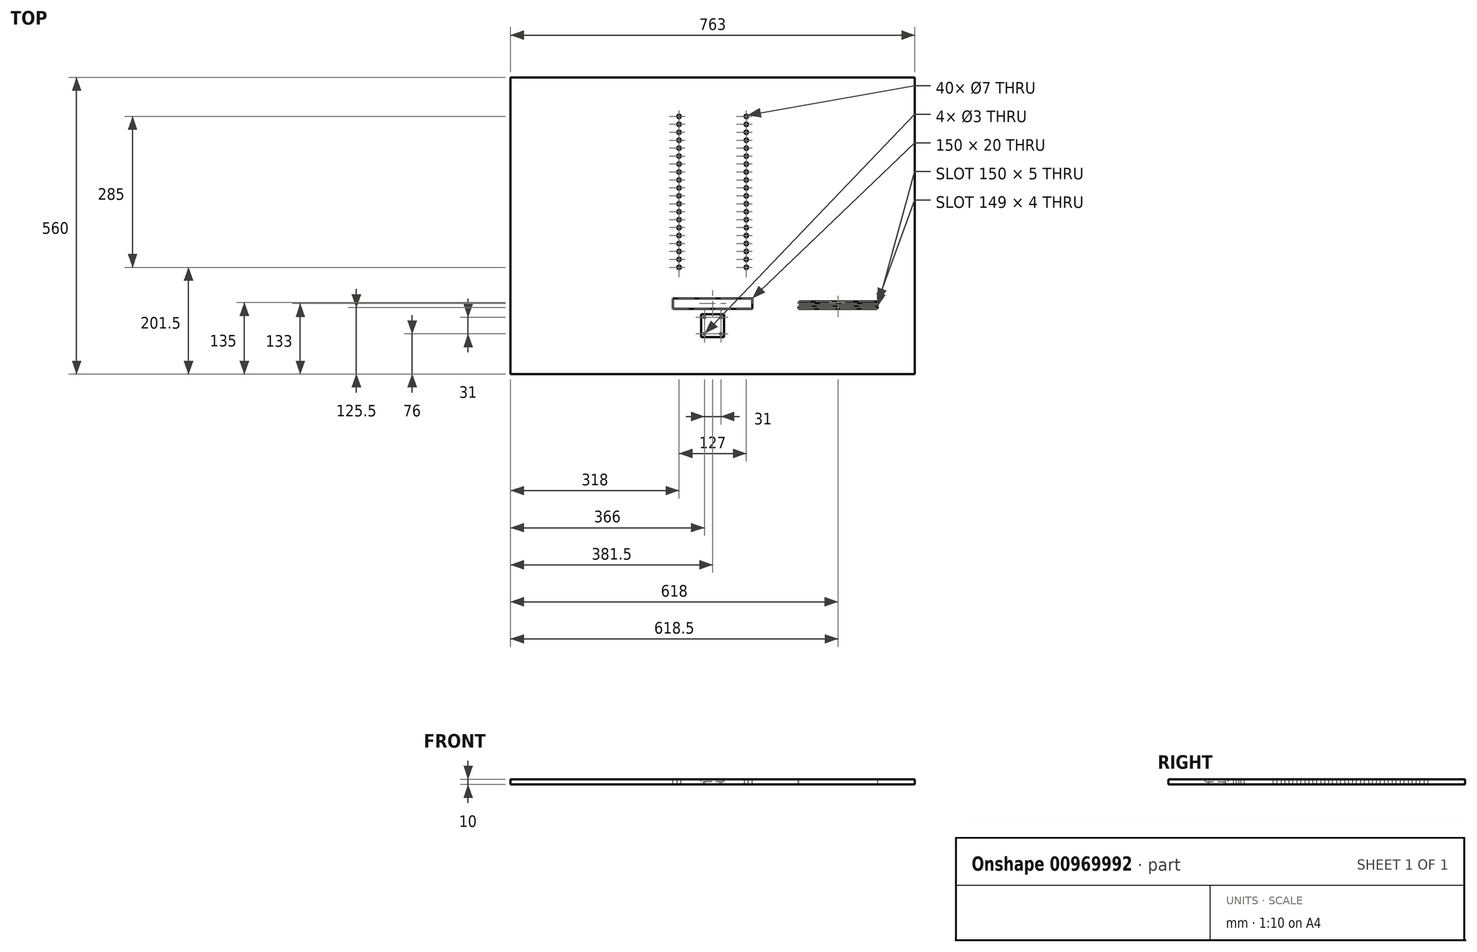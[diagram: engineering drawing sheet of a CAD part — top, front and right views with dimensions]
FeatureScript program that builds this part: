
annotation { "Feature Type Name" : "Feature", "Feature Type Description" : "" }
export const myFeature = defineFeature(function(context is Context, id is Id, definition is map)
    precondition{}
    {
        {
            var Q0;
            Q0=qCreatedBy(makeId("Top.planeOp"),FACE);
            var sketch = newSketch(context, id + "F0", { "sketchPlane" : qUnion([Q0])});
            skLineSegment(sketch, "E0.bottom", {"start": v(381.5, -280) * mm, "end": v(-381.5, -280) * mm});
            skLineSegment(sketch, "E0.top", {"start": v(381.5, 280) * mm, "end": v(-381.5, 280) * mm});
            skLineSegment(sketch, "E0.left", {"start": v(381.5, -280) * mm, "end": v(381.5, 280) * mm});
            skLineSegment(sketch, "E0.right", {"start": v(-381.5, -280) * mm, "end": v(-381.5, 280) * mm});
            skPoint(sketch, "E0.middle", {"position": v(0, 0) * mm});
            skSolve(sketch);
        }
        {
            var Q0;
            Q0=qSketchRegion(id+"F0",true);
            extrude(context, id + "F1", {"entities" : qUnion([Q0]), "depth" : 10 * mm, "offsetDistance" : 25 * mm});
        }
        {
            var Q0;
            Q0=makeQuery(id+"F1.opExtrude","CAP_FACE",FACE,{"disambiguationData":[OSD([sQuery(id+"F0.wireOp",EDGE,"E0.bottom"),sQuery(id+"F0.wireOp",EDGE,"E0.top"),sQuery(id+"F0.wireOp",EDGE,"E0.left"),sQuery(id+"F0.wireOp",EDGE,"E0.right")])],"isStart":false});
            var sketch = newSketch(context, id + "F2", { "sketchPlane" : qUnion([Q0])});
            skLineSegment(sketch, "E1", {"start": v(0, 280) * mm, "end": v(0, -280) * mm, "construction": true});
            skCircle(sketch, "E2", {"center": v(-63.5, 206.5) * mm, "radius": 3.5 * mm});
            skCircle(sketch, "E3.0.1.0", {"center": v(-63.5, 191.5) * mm, "radius": 3.5 * mm});
            skCircle(sketch, "E3.0.2.0", {"center": v(-63.5, 176.5) * mm, "radius": 3.5 * mm});
            skCircle(sketch, "E3.0.3.0", {"center": v(-63.5, 161.5) * mm, "radius": 3.5 * mm});
            skCircle(sketch, "E3.0.4.0", {"center": v(-63.5, 146.5) * mm, "radius": 3.5 * mm});
            skCircle(sketch, "E3.0.5.0", {"center": v(-63.5, 131.5) * mm, "radius": 3.5 * mm});
            skCircle(sketch, "E3.0.6.0", {"center": v(-63.5, 116.5) * mm, "radius": 3.5 * mm});
            skCircle(sketch, "E3.0.7.0", {"center": v(-63.5, 101.5) * mm, "radius": 3.5 * mm});
            skCircle(sketch, "E3.0.8.0", {"center": v(-63.5, 86.5) * mm, "radius": 3.5 * mm});
            skCircle(sketch, "E3.0.9.0", {"center": v(-63.5, 71.5) * mm, "radius": 3.5 * mm});
            skCircle(sketch, "E3.0.10.0", {"center": v(-63.5, 56.5) * mm, "radius": 3.5 * mm});
            skCircle(sketch, "E3.0.11.0", {"center": v(-63.5, 41.5) * mm, "radius": 3.5 * mm});
            skCircle(sketch, "E3.0.12.0", {"center": v(-63.5, 26.5) * mm, "radius": 3.5 * mm});
            skCircle(sketch, "E3.0.13.0", {"center": v(-63.5, 11.5) * mm, "radius": 3.5 * mm});
            skCircle(sketch, "E3.0.14.0", {"center": v(-63.5, -3.5) * mm, "radius": 3.5 * mm});
            skCircle(sketch, "E3.0.15.0", {"center": v(-63.5, -18.5) * mm, "radius": 3.5 * mm});
            skCircle(sketch, "E3.0.16.0", {"center": v(-63.5, -33.5) * mm, "radius": 3.5 * mm});
            skCircle(sketch, "E3.0.17.0", {"center": v(-63.5, -48.5) * mm, "radius": 3.5 * mm});
            skCircle(sketch, "E3.0.18.0", {"center": v(-63.5, -63.5) * mm, "radius": 3.5 * mm});
            skCircle(sketch, "E3.0.19.0", {"center": v(-63.5, -78.5) * mm, "radius": 3.5 * mm});
            skLineSegment(sketch, "E3.direction2", {"start": v(-63.5, 206.5) * mm, "end": v(-63.5, 191.5) * mm, "construction": true});
            skCircle(sketch, "E4.MirrorC", {"center": v(63.5, 191.5) * mm, "radius": 3.5 * mm});
            skCircle(sketch, "E5.MirrorC", {"center": v(63.5, 86.5) * mm, "radius": 3.5 * mm});
            skCircle(sketch, "E6.MirrorC", {"center": v(63.5, 41.5) * mm, "radius": 3.5 * mm});
            skCircle(sketch, "E7.MirrorC", {"center": v(63.5, 26.5) * mm, "radius": 3.5 * mm});
            skCircle(sketch, "E8.MirrorC", {"center": v(63.5, 101.5) * mm, "radius": 3.5 * mm});
            skCircle(sketch, "E9.MirrorC", {"center": v(63.5, -18.5) * mm, "radius": 3.5 * mm});
            skCircle(sketch, "E10.MirrorC", {"center": v(63.5, 131.5) * mm, "radius": 3.5 * mm});
            skCircle(sketch, "E11.MirrorC", {"center": v(63.5, -63.5) * mm, "radius": 3.5 * mm});
            skCircle(sketch, "E12.MirrorC", {"center": v(63.5, 71.5) * mm, "radius": 3.5 * mm});
            skCircle(sketch, "E13.MirrorC", {"center": v(63.5, 161.5) * mm, "radius": 3.5 * mm});
            skCircle(sketch, "E14.MirrorC", {"center": v(63.5, 176.5) * mm, "radius": 3.5 * mm});
            skCircle(sketch, "E15.MirrorC", {"center": v(63.5, -48.5) * mm, "radius": 3.5 * mm});
            skCircle(sketch, "E16.MirrorC", {"center": v(63.5, 11.5) * mm, "radius": 3.5 * mm});
            skCircle(sketch, "E17.MirrorC", {"center": v(63.5, -78.5) * mm, "radius": 3.5 * mm});
            skCircle(sketch, "E18.MirrorC", {"center": v(63.5, -33.5) * mm, "radius": 3.5 * mm});
            skCircle(sketch, "E19.MirrorC", {"center": v(63.5, 146.5) * mm, "radius": 3.5 * mm});
            skCircle(sketch, "E20.MirrorC", {"center": v(63.5, -3.5) * mm, "radius": 3.5 * mm});
            skCircle(sketch, "E21.MirrorC", {"center": v(63.5, 116.5) * mm, "radius": 3.5 * mm});
            skCircle(sketch, "E22.MirrorC", {"center": v(63.5, 56.5) * mm, "radius": 3.5 * mm});
            skCircle(sketch, "E23.MirrorC", {"center": v(63.5, 206.5) * mm, "radius": 3.5 * mm});
            skSolve(sketch);
        }
        {
            var Q0;
            Q0=qSketchRegion(id+"F2",true);
            extrude(context, id + "F3", {"entities" : qUnion([Q0]), "operationType" : NewBodyOperationType.REMOVE, "oppositeDirection" : true, "depth" : 10 * mm, "offsetDistance" : 25 * mm});
        }
        {
            var Q0;
            Q0=makeQuery(id+"F1.opExtrude","CAP_FACE",FACE,{"disambiguationData":[OSD([sQuery(id+"F0.wireOp",EDGE,"E0.bottom"),sQuery(id+"F0.wireOp",EDGE,"E0.top"),sQuery(id+"F0.wireOp",EDGE,"E0.left"),sQuery(id+"F0.wireOp",EDGE,"E0.right")])],"isStart":false});
            var sketch = newSketch(context, id + "F4", { "sketchPlane" : qUnion([Q0])});
            skLineSegment(sketch, "E24", {"start": v(0, 280) * mm, "end": v(0, -280) * mm, "construction": true});
            skLineSegment(sketch, "E25.bottom", {"start": v(75, -137) * mm, "end": v(-75, -137) * mm});
            skLineSegment(sketch, "E25.top", {"start": v(75, -157) * mm, "end": v(-75, -157) * mm});
            skLineSegment(sketch, "E25.left", {"start": v(75, -137) * mm, "end": v(75, -157) * mm});
            skLineSegment(sketch, "E25.right", {"start": v(-75, -137) * mm, "end": v(-75, -157) * mm});
            skPoint(sketch, "E25.middle", {"position": v(0, -147) * mm});
            skLineSegment(sketch, "E26.bottom", {"start": v(21.5, -210) * mm, "end": v(-21.5, -210) * mm});
            skLineSegment(sketch, "E26.top", {"start": v(21.5, -167) * mm, "end": v(-21.5, -167) * mm});
            skLineSegment(sketch, "E26.left", {"start": v(21.5, -210) * mm, "end": v(21.5, -167) * mm});
            skLineSegment(sketch, "E26.right", {"start": v(-21.5, -210) * mm, "end": v(-21.5, -167) * mm});
            skPoint(sketch, "E26.middle", {"position": v(0, -188.5) * mm});
            skCircle(sketch, "E27", {"center": v(-15.5, -173) * mm, "radius": 1.5 * mm});
            skCircle(sketch, "E28", {"center": v(15.5, -173) * mm, "radius": 1.5 * mm});
            skCircle(sketch, "E29", {"center": v(15.5, -204) * mm, "radius": 1.5 * mm});
            skCircle(sketch, "E30", {"center": v(-15.5, -204) * mm, "radius": 1.5 * mm});
            skLineSegment(sketch, "E31", {"start": v(381.5, -147) * mm, "end": v(-381.5, -147) * mm, "construction": true});
            skLineSegment(sketch, "E32.bottom", {"start": v(164, -152) * mm, "end": v(309, -152) * mm});
            skLineSegment(sketch, "E32.top", {"start": v(164, -157) * mm, "end": v(309, -157) * mm});
            skLineSegment(sketch, "E33.bottom", {"start": v(164.5, -147) * mm, "end": v(309.5, -147) * mm});
            skLineSegment(sketch, "E33.top", {"start": v(164.5, -143) * mm, "end": v(309.5, -143) * mm});
            skArc(sketch, "E34", {"start": v(164.5, -143) * mm, "mid": v(162.5, -145) * mm, "end": v(164.5, -147) * mm});
            skArc(sketch, "E35", {"start": v(309.5, -147) * mm, "mid": v(311.5, -145) * mm, "end": v(309.5, -143) * mm});
            skArc(sketch, "E36", {"start": v(164, -152) * mm, "mid": v(161.5, -154.5) * mm, "end": v(164, -157) * mm});
            skArc(sketch, "E37", {"start": v(309, -157) * mm, "mid": v(311.5, -154.5) * mm, "end": v(309, -152) * mm});
            skCircle(sketch, "E38", {"center": v(-341.5, 0) * mm, "radius": 3.5 * mm});
            skCircle(sketch, "E39", {"center": v(-166.5, -238) * mm, "radius": 3.5 * mm});
            skCircle(sketch, "E40", {"center": v(179.5, -238) * mm, "radius": 3.5 * mm});
            skCircle(sketch, "E41", {"center": v(338.5, 2) * mm, "radius": 3.5 * mm});
            skCircle(sketch, "E42", {"center": v(167.5, 237.5) * mm, "radius": 3.5 * mm});
            skCircle(sketch, "E43", {"center": v(-176.5, 239) * mm, "radius": 3.5 * mm});
            skSolve(sketch);
        }
        {
            var Q0;
            Q0=makeQuery(id+"F4.imprint","IMPRINT",FACE,{"disambiguationData":[TD([[makeQuery(id+"F4.imprint","IMPRINT",EDGE,{"derivedFrom":sQuery(id+"F4.wireOp",EDGE,"E26.bottom")}),-1.0]])]});
            extrude(context, id + "F5", {"entities" : qUnion([Q0]), "operationType" : NewBodyOperationType.REMOVE, "oppositeDirection" : true, "depth" : 5 * mm, "offsetDistance" : 25 * mm});
        }
        {
            var Q0;
            Q0=makeQuery(id+"F5.boolean.opBoolean","SPLIT",FACE,{"disambiguationData":[TD([makeQuery(id+"F5.opExtrude","SWEPT_FACE",FACE,{"disambiguationData":[OSD([sQuery(id+"F4.wireOp",EDGE,"E29")])]})])],"derivedFrom":makeQuery(id+"F1.opExtrude","CAP_FACE",FACE,{"disambiguationData":[OSD([sQuery(id+"F0.wireOp",EDGE,"E0.bottom"),sQuery(id+"F0.wireOp",EDGE,"E0.top"),sQuery(id+"F0.wireOp",EDGE,"E0.left"),sQuery(id+"F0.wireOp",EDGE,"E0.right")])],"isStart":false})});
            var Q1;
            Q1=makeQuery(id+"F5.boolean.opBoolean","SPLIT",FACE,{"disambiguationData":[TD([makeQuery(id+"F5.opExtrude","SWEPT_FACE",FACE,{"disambiguationData":[OSD([sQuery(id+"F4.wireOp",EDGE,"E28")])]})])],"derivedFrom":makeQuery(id+"F1.opExtrude","CAP_FACE",FACE,{"disambiguationData":[OSD([sQuery(id+"F0.wireOp",EDGE,"E0.bottom"),sQuery(id+"F0.wireOp",EDGE,"E0.top"),sQuery(id+"F0.wireOp",EDGE,"E0.left"),sQuery(id+"F0.wireOp",EDGE,"E0.right")])],"isStart":false})});
            var Q2;
            Q2=makeQuery(id+"F5.boolean.opBoolean","SPLIT",FACE,{"disambiguationData":[TD([makeQuery(id+"F5.opExtrude","SWEPT_FACE",FACE,{"disambiguationData":[OSD([sQuery(id+"F4.wireOp",EDGE,"E27")])]})])],"derivedFrom":makeQuery(id+"F1.opExtrude","CAP_FACE",FACE,{"disambiguationData":[OSD([sQuery(id+"F0.wireOp",EDGE,"E0.bottom"),sQuery(id+"F0.wireOp",EDGE,"E0.top"),sQuery(id+"F0.wireOp",EDGE,"E0.left"),sQuery(id+"F0.wireOp",EDGE,"E0.right")])],"isStart":false})});
            var Q3;
            Q3=makeQuery(id+"F5.boolean.opBoolean","SPLIT",FACE,{"disambiguationData":[TD([makeQuery(id+"F5.opExtrude","SWEPT_FACE",FACE,{"disambiguationData":[OSD([sQuery(id+"F4.wireOp",EDGE,"E30")])]})])],"derivedFrom":makeQuery(id+"F1.opExtrude","CAP_FACE",FACE,{"disambiguationData":[OSD([sQuery(id+"F0.wireOp",EDGE,"E0.bottom"),sQuery(id+"F0.wireOp",EDGE,"E0.top"),sQuery(id+"F0.wireOp",EDGE,"E0.left"),sQuery(id+"F0.wireOp",EDGE,"E0.right")])],"isStart":false})});
            extrude(context, id + "F6", {"entities" : qUnion([Q0, Q1, Q2, Q3]), "operationType" : NewBodyOperationType.REMOVE, "oppositeDirection" : true, "depth" : 10 * mm, "offsetDistance" : 25 * mm});
        }
        {
            var Q0;
            Q0=makeQuery(id+"F4.imprint","IMPRINT",FACE,{"disambiguationData":[TD([[makeQuery(id+"F4.imprint","IMPRINT",EDGE,{"derivedFrom":sQuery(id+"F4.wireOp",EDGE,"E25.bottom")}),1.0]])]});
            extrude(context, id + "F7", {"entities" : qUnion([Q0]), "operationType" : NewBodyOperationType.REMOVE, "oppositeDirection" : true, "depth" : 10 * mm, "offsetDistance" : 25 * mm});
        }
        {
            var Q0;
            Q0=makeQuery(id+"F4.imprint","IMPRINT",FACE,{"disambiguationData":[TD([[makeQuery(id+"F4.imprint","IMPRINT",EDGE,{"derivedFrom":sQuery(id+"F4.wireOp",EDGE,"E32.bottom")}),-1.0]])]});
            extrude(context, id + "F8", {"entities" : qUnion([Q0]), "operationType" : NewBodyOperationType.REMOVE, "oppositeDirection" : true, "depth" : 10 * mm, "offsetDistance" : 25 * mm});
        }
        {
            var Q0;
            Q0=makeQuery(id+"F4.imprint","IMPRINT",FACE,{"disambiguationData":[TD([[makeQuery(id+"F4.imprint","IMPRINT",EDGE,{"derivedFrom":sQuery(id+"F4.wireOp",EDGE,"E33.bottom")}),1.0]])]});
            extrude(context, id + "F9", {"entities" : qUnion([Q0]), "operationType" : NewBodyOperationType.REMOVE, "oppositeDirection" : true, "depth" : 10 * mm, "offsetDistance" : 25 * mm});
        }
        {
            var Q0;
            Q0=qSketchRegion(id+"F2",true);
            extrude(context, id + "F10", {"entities" : qUnion([Q0]), "operationType" : NewBodyOperationType.REMOVE, "oppositeDirection" : true, "depth" : 10 * mm, "offsetDistance" : 25 * mm});
        }
    });
